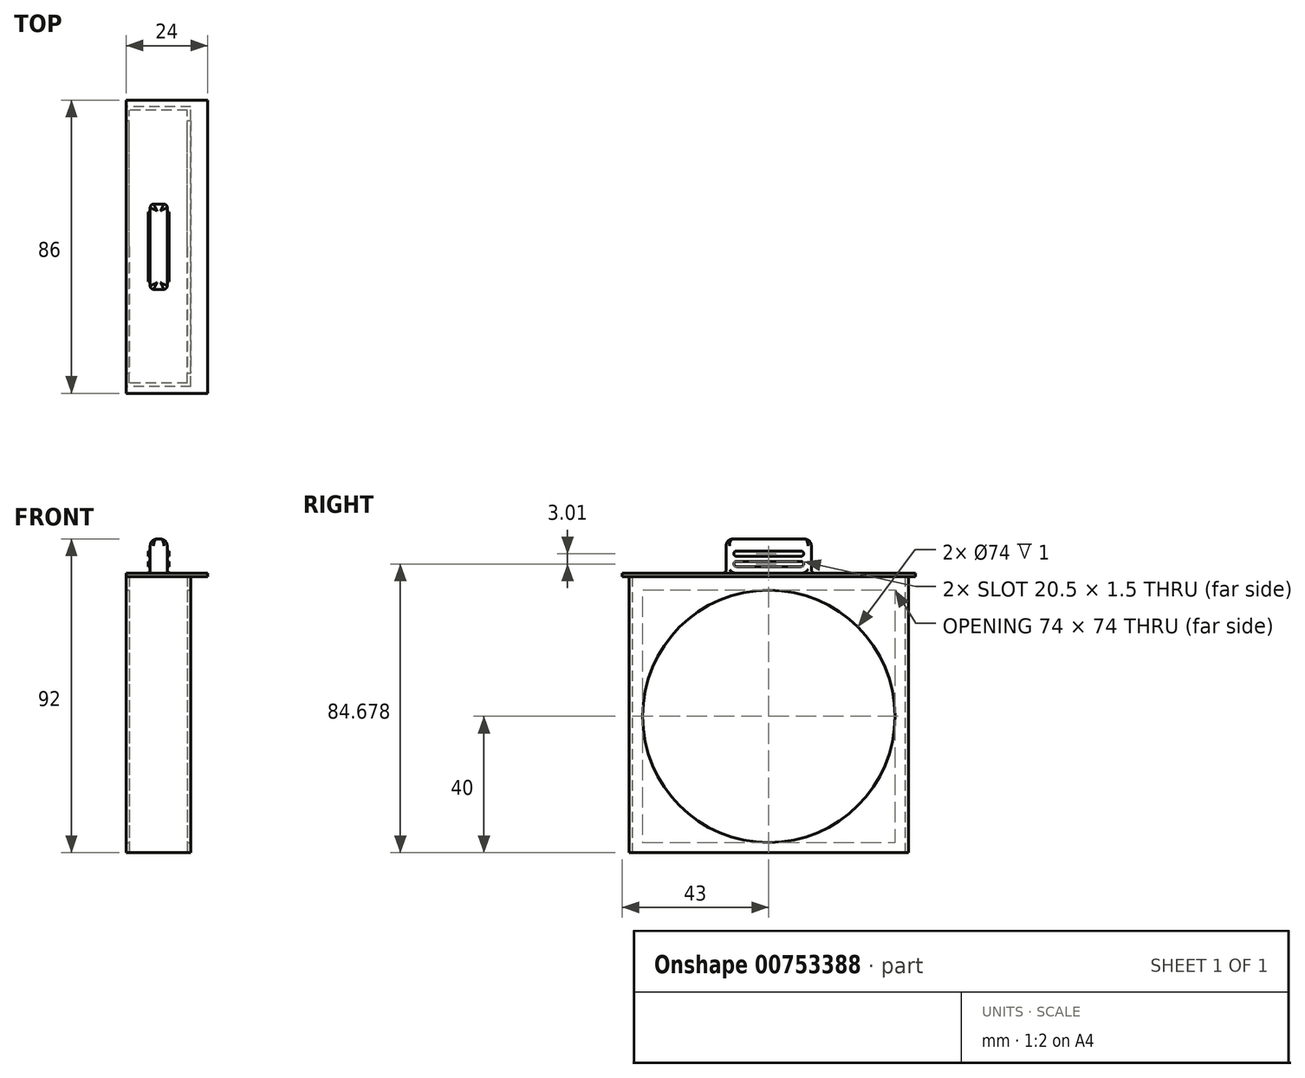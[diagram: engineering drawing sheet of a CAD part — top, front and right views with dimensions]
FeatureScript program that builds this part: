
annotation { "Feature Type Name" : "Feature", "Feature Type Description" : "" }
export const myFeature = defineFeature(function(context is Context, id is Id, definition is map)
    precondition{}
    {
        {
            var Q0;
            Q0=qCreatedBy(makeId("Right.planeOp"),FACE);
            var sketch = newSketch(context, id + "F0", { "sketchPlane" : qUnion([Q0])});
            skLineSegment(sketch, "E0.bottom", {"start": v(-41, 41) * mm, "end": v(41, 41) * mm});
            skLineSegment(sketch, "E0.top", {"start": v(-41, -40) * mm, "end": v(41, -40) * mm});
            skLineSegment(sketch, "E0.left", {"start": v(-41, 41) * mm, "end": v(-41, -40) * mm});
            skLineSegment(sketch, "E0.right", {"start": v(41, 41) * mm, "end": v(41, -40) * mm});
            skSolve(sketch);
        }
        {
            var Q0;
            Q0 = qSketchRegion(id + "F0", true);
            extrude(context, id + "F1", {"entities" : qUnion([Q0]), "depth" : 19 * mm, "offsetDistance" : 25 * mm});
        }
        {
            var Q0;
            Q0=makeQuery(id+"F1.opExtrude","CAP_FACE",FACE,{"disambiguationData":[OSD([sQuery(id+"F0.wireOp",EDGE,"E0.bottom"),sQuery(id+"F0.wireOp",EDGE,"E0.top"),sQuery(id+"F0.wireOp",EDGE,"E0.left"),sQuery(id+"F0.wireOp",EDGE,"E0.right")])],"isStart":false});
            var sketch = newSketch(context, id + "F2", { "sketchPlane" : qUnion([Q0])});
            skCircle(sketch, "E1", {"center": v(0, 0) * mm, "radius": 37 * mm});
            skSolve(sketch);
        }
        {
            var Q0;
            Q0 = qSketchRegion(id + "F2", true);
            extrude(context, id + "F3", {"entities" : qUnion([Q0]), "operationType" : NewBodyOperationType.REMOVE, "oppositeDirection" : true, "depth" : 25 * mm, "offsetDistance" : 25 * mm});
        }
        {
            var Q0;
            Q0=makeQuery(id+"F1.opExtrude","SWEPT_FACE",FACE,{"disambiguationData":[OSD([sQuery(id+"F0.wireOp",EDGE,"E0.top")])]});
            var sketch = newSketch(context, id + "F4", { "sketchPlane" : qUnion([Q0])});
            skLineSegment(sketch, "E2.bottom", {"start": v(18, 40) * mm, "end": v(1, 40) * mm});
            skLineSegment(sketch, "E2.top", {"start": v(18, -40) * mm, "end": v(1, -40) * mm});
            skLineSegment(sketch, "E2.left", {"start": v(18, 40) * mm, "end": v(18, -40) * mm});
            skLineSegment(sketch, "E2.right", {"start": v(1, 40) * mm, "end": v(1, -40) * mm});
            skSolve(sketch);
        }
        {
            var Q0;
            Q0 = qSketchRegion(id + "F4", true);
            extrude(context, id + "F5", {"entities" : qUnion([Q0]), "operationType" : NewBodyOperationType.REMOVE, "oppositeDirection" : true, "depth" : 81 * mm, "offsetDistance" : 25 * mm});
        }
        {
            var Q0;
            Q0=makeQuery(id+"F1.opExtrude","SWEPT_FACE",FACE,{"disambiguationData":[OSD([sQuery(id+"F0.wireOp",EDGE,"E0.bottom")])]});
            var sketch = newSketch(context, id + "F6", { "sketchPlane" : qUnion([Q0])});
            skLineSegment(sketch, "E3.bottom", {"start": v(0, 43) * mm, "end": v(24, 43) * mm});
            skLineSegment(sketch, "E3.top", {"start": v(0, -43) * mm, "end": v(24, -43) * mm});
            skLineSegment(sketch, "E3.left", {"start": v(0, 43) * mm, "end": v(0, -43) * mm});
            skLineSegment(sketch, "E3.right", {"start": v(24, 43) * mm, "end": v(24, -43) * mm});
            skSolve(sketch);
        }
        {
            var Q0;
            Q0 = qSketchRegion(id + "F6", true);
            extrude(context, id + "F7", {"entities" : qUnion([Q0]), "operationType" : NewBodyOperationType.ADD, "depth" : 1 * mm, "offsetDistance" : 25 * mm});
        }
        {
            var Q0;
            Q0=makeQuery(id+"F7.opExtrude","CAP_FACE",FACE,{"disambiguationData":[OSD([sQuery(id+"F6.wireOp",EDGE,"E3.bottom"),sQuery(id+"F6.wireOp",EDGE,"E3.top"),sQuery(id+"F6.wireOp",EDGE,"E3.left"),sQuery(id+"F6.wireOp",EDGE,"E3.right")])],"isStart":false});
            var sketch = newSketch(context, id + "F8", { "sketchPlane" : qUnion([Q0])});
            skLineSegment(sketch, "E4.bottom", {"start": v(7.1, 12.5) * mm, "end": v(12.1, 12.5) * mm});
            skLineSegment(sketch, "E4.top", {"start": v(7.1, -12.5) * mm, "end": v(12.1, -12.5) * mm});
            skLineSegment(sketch, "E4.left", {"start": v(7.1, 12.5) * mm, "end": v(7.1, -12.5) * mm});
            skLineSegment(sketch, "E4.right", {"start": v(12.1, 12.5) * mm, "end": v(12.1, -12.5) * mm});
            skSolve(sketch);
        }
        {
            var Q0;
            Q0 = qSketchRegion(id + "F8", true);
            extrude(context, id + "F9", {"entities" : qUnion([Q0]), "operationType" : NewBodyOperationType.ADD, "depth" : 10 * mm, "offsetDistance" : 25 * mm});
        }
        {
            var Q0;
            Q0=makeQuery(id+"F9.opExtrude","CAP_FACE",FACE,{"disambiguationData":[OSD([sQuery(id+"F8.wireOp",EDGE,"E4.bottom"),sQuery(id+"F8.wireOp",EDGE,"E4.top"),sQuery(id+"F8.wireOp",EDGE,"E4.left"),sQuery(id+"F8.wireOp",EDGE,"E4.right")])],"isStart":false});
            fillet(context, id + "F10", {"entities" : qUnion([Q0]), "radius" : 2 * mm, "tangentPropagation" : true, "allowEdgeOverflow" : false});
        }
        {
            var Q0;
            Q0=makeQuery(id+"F9.opExtrude","SWEPT_FACE",FACE,{"disambiguationData":[OSD([sQuery(id+"F8.wireOp",EDGE,"E4.top")])]});
            var Q1;
            Q1=makeQuery(id+"F9.opExtrude","SWEPT_FACE",FACE,{"disambiguationData":[OSD([sQuery(id+"F8.wireOp",EDGE,"E4.bottom")])]});
            fillet(context, id + "F11", {"entities" : qUnion([Q0, Q1]), "radius" : 1 * mm, "tangentPropagation" : true, "allowEdgeOverflow" : false});
        }
        {
            var Q0;
            Q0=makeQuery(id+"F9.opExtrude","SWEPT_FACE",FACE,{"disambiguationData":[OSD([sQuery(id+"F8.wireOp",EDGE,"E4.left")])]});
            var sketch = newSketch(context, id + "F12", { "sketchPlane" : qUnion([Q0])});
            skLineSegment(sketch, "E5.bottom", {"start": v(-9.5, 48.44) * mm, "end": v(9.5, 48.44) * mm});
            skLineSegment(sketch, "E5.top", {"start": v(-9.5, 46.94) * mm, "end": v(9.5, 46.94) * mm});
            skLineSegment(sketch, "E5.left", {"start": v(-9.5, 48.44) * mm, "end": v(-9.5, 46.94) * mm});
            skLineSegment(sketch, "E5.right", {"start": v(9.5, 48.44) * mm, "end": v(9.5, 46.94) * mm});
            skLineSegment(sketch, "E6.bottom", {"start": v(-9.5, 45.43) * mm, "end": v(9.5, 45.43) * mm});
            skLineSegment(sketch, "E6.top", {"start": v(-9.5, 43.93) * mm, "end": v(9.5, 43.93) * mm});
            skLineSegment(sketch, "E6.left", {"start": v(-9.5, 45.43) * mm, "end": v(-9.5, 43.93) * mm});
            skLineSegment(sketch, "E6.right", {"start": v(9.5, 45.43) * mm, "end": v(9.5, 43.93) * mm});
            skArc(sketch, "E7", {"start": v(-9.5, 48.44) * mm, "mid": v(-10.25, 47.69) * mm, "end": v(-9.5, 46.94) * mm});
            skArc(sketch, "E8", {"start": v(9.5, 46.94) * mm, "mid": v(10.25, 47.69) * mm, "end": v(9.5, 48.44) * mm});
            skArc(sketch, "E9", {"start": v(-9.5, 45.43) * mm, "mid": v(-10.25, 44.68) * mm, "end": v(-9.5, 43.93) * mm});
            skArc(sketch, "E10", {"start": v(9.5, 43.93) * mm, "mid": v(10.25, 44.68) * mm, "end": v(9.5, 45.43) * mm});
            skSolve(sketch);
        }
        {
            var Q0;
            Q0 = qSketchRegion(id + "F12", true);
            extrude(context, id + "F13", {"entities" : qUnion([Q0]), "operationType" : NewBodyOperationType.ADD, "depth" : .5 * mm, "offsetDistance" : 25 * mm, "hasSecondDirection" : true, "secondDirectionOppositeDirection" : true, "secondDirectionDepth" : 5.5 * mm});
        }
    });
